# Revit family: SAE105
name_source: partatom
category: Lighting Fixtures
revit_build: Autodesk Revit 2013 (Build: 20130531_2115(x64)
units: mm (PartAtom-declared; Revit-internal decimal feet)

## types (3) — shared parameters
Apparent Load = 0 VA
Assembly Code = D5020200
Color Filter = 16777215
Default Elevation = 4' - 0"
Description = Linear Pendant Indirect
Dimming Lamp Color Temperature Shift = <None>
Emit Shape Visible in Rendering = No
Emit from Rectangle Width = 0' - 4"
Glass = Hubbell - White Glass
Housing Material = Paint - Hubbell - Matte White
Lamp = LED's
Load Classification = Lighting
Manufacturer = Litecontrol Lighting
Model = SAE105
Photometric Notes = More IES files download on Photometric Web Link
Photometric Web Link = https://www.hubbell.com
Power Factor = 1
Product Page URL = https://www.hubbell.com
Tilt Angle = -90.00°
URL = http://www.litecontrol.com
Voltage = 120 V
Warranty = 5-Years Warranty
Wattage Comments = Up to 131 lumens/watt efficacy

## per-type parameters (varying)
| type | Emit from Rectangle Length | Photometric Web File | zz Length 1 |
| SAE105-04 | 3' - 10" | SAE105-P-LPA-SQ-4-35K-155.IES | 4' - 0" |
| SAE105-08 | 7' - 10" | SAE105-P-LPA-PF-4-35K-155.IES | 8' - 0" |
| SAE105-12 | 11' - 10" | SAE105-P-LPA-PF-4-35K-155.IES | 12' - 0" |

## geometry (parser evidence)
native form markers: Sweep x4
no freeform markers — native parametric forms only
